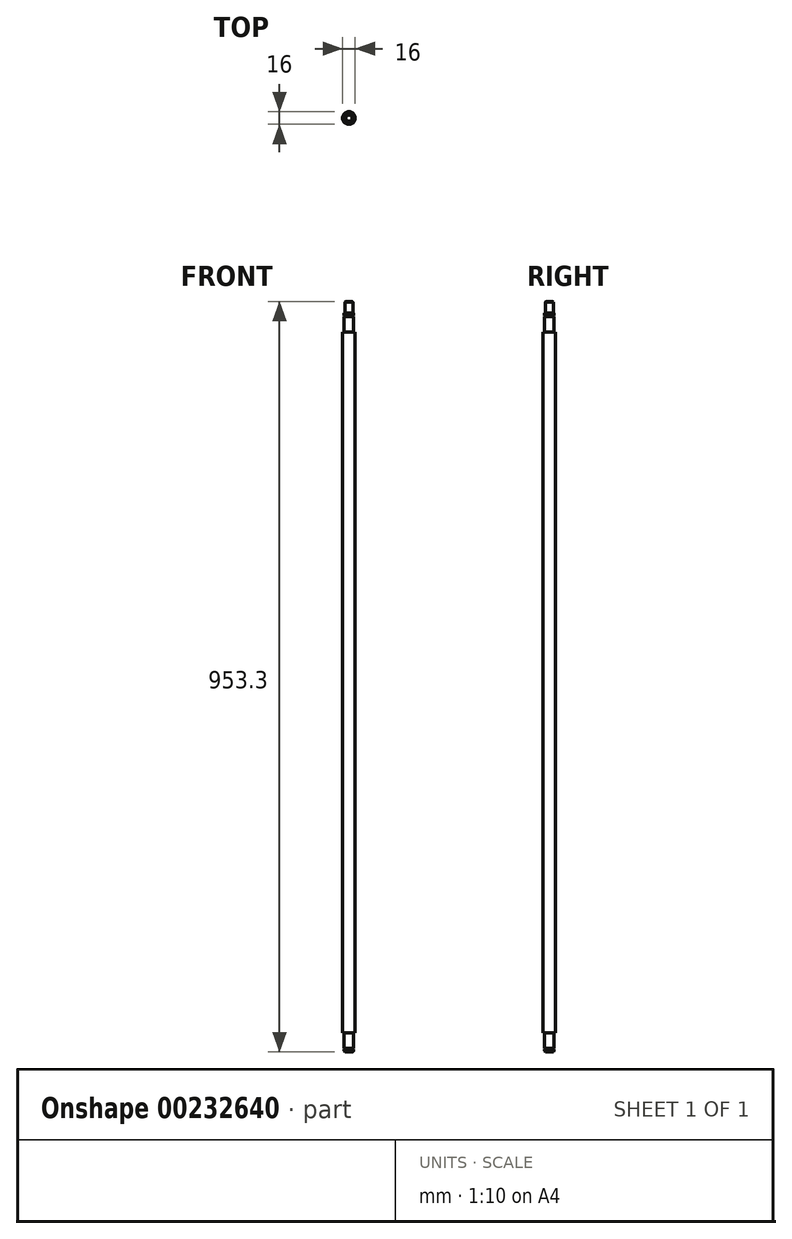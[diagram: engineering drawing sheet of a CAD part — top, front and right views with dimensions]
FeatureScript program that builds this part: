
annotation { "Feature Type Name" : "Feature", "Feature Type Description" : "" }
export const myFeature = defineFeature(function(context is Context, id is Id, definition is map)
    precondition{}
    {
        {
            var Q0;
            Q0=qCreatedBy(makeId("Top.planeOp"),FACE);
            var sketch = newSketch(context, id + "F0", { "sketchPlane" : qUnion([Q0])});
            skCircle(sketch, "E0", {"center": v(0, 0) * mm, "radius": 6 * mm});
            skSolve(sketch);
        }
        {
            var Q0;
            Q0=makeQuery(id+"F0.imprint","IMPRINT",FACE,{"disambiguationData":[TD([[makeQuery(id+"F0.imprint","IMPRINT",EDGE,{"derivedFrom":sQuery(id+"F0.wireOp",EDGE,"E0")}),1.0]])]});
            extrude(context, id + "F1", {"entities" : qUnion([Q0]), "depth" : 3 * mm});
        }
        {
            var Q0;
            Q0=makeQuery(id+"F1.opExtrude","CAP_FACE",FACE,{"disambiguationData":[OSD([sQuery(id+"F0.wireOp",EDGE,"E0")])],"isStart":false});
            var sketch = newSketch(context, id + "F2", { "sketchPlane" : qUnion([Q0])});
            skCircle(sketch, "E1", {"center": v(0, 0) * mm, "radius": 4.8 * mm});
            skSolve(sketch);
        }
        {
            var Q0;
            Q0=makeQuery(id+"F2.imprint","IMPRINT",FACE,{"disambiguationData":[TD([[makeQuery(id+"F2.imprint","IMPRINT",EDGE,{"derivedFrom":sQuery(id+"F2.wireOp",EDGE,"E1")}),1.0]])]});
            extrude(context, id + "F3", {"entities" : qUnion([Q0]), "operationType" : NewBodyOperationType.ADD, "depth" : 1.15 * mm});
        }
        {
            var Q0;
            Q0=makeQuery(id+"F3.opExtrude","CAP_FACE",FACE,{"disambiguationData":[OSD([sQuery(id+"F2.wireOp",EDGE,"E1")])],"isStart":false});
            var sketch = newSketch(context, id + "F4", { "sketchPlane" : qUnion([Q0])});
            skCircle(sketch, "E2", {"center": v(0, 0) * mm, "radius": 6 * mm});
            skSolve(sketch);
        }
        {
            var Q0;
            Q0=makeQuery(id+"F4.imprint","IMPRINT",FACE,{"disambiguationData":[TD([[makeQuery(id+"F4.imprint","IMPRINT",EDGE,{"derivedFrom":sQuery(id+"F4.wireOp",EDGE,"E2")}),1.0]])]});
            var Q1;
            Q1=makeQuery(id+"F4.imprint","IMPRINT",FACE,{"disambiguationData":[TD([[makeQuery(id+"F4.imprint","IMPRINT",EDGE,{"derivedFrom":makeQuery(id+"F3.opExtrude","CAP_EDGE",EDGE,{"disambiguationData":[OSD([sQuery(id+"F2.wireOp",EDGE,"E1")])],"isStart":false})}),1.0]])]});
            extrude(context, id + "F5", {"entities" : qUnion([Q0, Q1]), "operationType" : NewBodyOperationType.ADD, "depth" : 20 * mm});
        }
        {
            var Q0;
            Q0=makeQuery(id+"F5.opExtrude","CAP_FACE",FACE,{"disambiguationData":[OSD([sQuery(id+"F4.wireOp",EDGE,"E2")])],"isStart":false});
            var sketch = newSketch(context, id + "F6", { "sketchPlane" : qUnion([Q0])});
            skCircle(sketch, "E3", {"center": v(0, 0) * mm, "radius": 8 * mm});
            skSolve(sketch);
        }
        {
            var Q0;
            Q0=makeQuery(id+"F6.imprint","IMPRINT",FACE,{"disambiguationData":[TD([[makeQuery(id+"F6.imprint","IMPRINT",EDGE,{"derivedFrom":sQuery(id+"F6.wireOp",EDGE,"E3")}),1.0]])]});
            var Q1;
            Q1=makeQuery(id+"F6.imprint","IMPRINT",FACE,{"disambiguationData":[TD([[makeQuery(id+"F6.imprint","IMPRINT",EDGE,{"derivedFrom":makeQuery(id+"F5.opExtrude","CAP_EDGE",EDGE,{"disambiguationData":[OSD([sQuery(id+"F4.wireOp",EDGE,"E2")])],"isStart":false})}),1.0]])]});
            extrude(context, id + "F7", {"entities" : qUnion([Q0, Q1]), "operationType" : NewBodyOperationType.ADD, "depth" : 890 * mm});
        }
        {
            var Q0;
            Q0=makeQuery(id+"F7.opExtrude","CAP_FACE",FACE,{"disambiguationData":[OSD([sQuery(id+"F6.wireOp",EDGE,"E3")])],"isStart":false});
            var sketch = newSketch(context, id + "F8", { "sketchPlane" : qUnion([Q0])});
            skCircle(sketch, "E4", {"center": v(0, 0) * mm, "radius": 6 * mm});
            skSolve(sketch);
        }
        {
            var Q0;
            Q0=makeQuery(id+"F8.imprint","IMPRINT",FACE,{"disambiguationData":[TD([[makeQuery(id+"F8.imprint","IMPRINT",EDGE,{"derivedFrom":sQuery(id+"F8.wireOp",EDGE,"E4")}),1.0]])]});
            extrude(context, id + "F9", {"entities" : qUnion([Q0]), "operationType" : NewBodyOperationType.ADD, "depth" : 20 * mm});
        }
        {
            var Q0;
            Q0=makeQuery(id+"F9.opExtrude","CAP_FACE",FACE,{"disambiguationData":[OSD([sQuery(id+"F8.wireOp",EDGE,"E4")])],"isStart":false});
            var sketch = newSketch(context, id + "F10", { "sketchPlane" : qUnion([Q0])});
            skCircle(sketch, "E5", {"center": v(0, 0) * mm, "radius": 4.8 * mm});
            skSolve(sketch);
        }
        {
            var Q0;
            Q0=makeQuery(id+"F10.imprint","IMPRINT",FACE,{"disambiguationData":[TD([[makeQuery(id+"F10.imprint","IMPRINT",EDGE,{"derivedFrom":sQuery(id+"F10.wireOp",EDGE,"E5")}),1.0]])]});
            extrude(context, id + "F11", {"entities" : qUnion([Q0]), "operationType" : NewBodyOperationType.ADD, "depth" : 1.15 * mm});
        }
        {
            var Q0;
            Q0=makeQuery(id+"F11.opExtrude","CAP_FACE",FACE,{"disambiguationData":[OSD([sQuery(id+"F10.wireOp",EDGE,"E5")])],"isStart":false});
            var sketch = newSketch(context, id + "F12", { "sketchPlane" : qUnion([Q0])});
            skCircle(sketch, "E6", {"center": v(0, 0) * mm, "radius": 6 * mm});
            skSolve(sketch);
        }
        {
            var Q0;
            Q0=makeQuery(id+"F12.imprint","IMPRINT",FACE,{"disambiguationData":[TD([[makeQuery(id+"F12.imprint","IMPRINT",EDGE,{"derivedFrom":makeQuery(id+"F11.opExtrude","CAP_EDGE",EDGE,{"disambiguationData":[OSD([sQuery(id+"F10.wireOp",EDGE,"E5")])],"isStart":false})}),1.0]])]});
            var Q1;
            Q1=makeQuery(id+"F12.imprint","IMPRINT",FACE,{"disambiguationData":[TD([[makeQuery(id+"F12.imprint","IMPRINT",EDGE,{"derivedFrom":sQuery(id+"F12.wireOp",EDGE,"E6")}),1.0]])]});
            extrude(context, id + "F13", {"entities" : qUnion([Q0, Q1]), "operationType" : NewBodyOperationType.ADD, "depth" : 3 * mm});
        }
        {
            var Q0;
            Q0=makeQuery(id+"F13.opExtrude","CAP_FACE",FACE,{"disambiguationData":[OSD([sQuery(id+"F12.wireOp",EDGE,"E6")])],"isStart":false});
            var sketch = newSketch(context, id + "F14", { "sketchPlane" : qUnion([Q0])});
            skCircle(sketch, "E7", {"center": v(0, 0) * mm, "radius": 5 * mm});
            skSolve(sketch);
        }
        {
            var Q0;
            Q0=makeQuery(id+"F14.imprint","IMPRINT",FACE,{"disambiguationData":[TD([[makeQuery(id+"F14.imprint","IMPRINT",EDGE,{"derivedFrom":sQuery(id+"F14.wireOp",EDGE,"E7")}),1.0]])]});
            extrude(context, id + "F15", {"entities" : qUnion([Q0]), "operationType" : NewBodyOperationType.ADD, "depth" : 15 * mm});
        }
        {
            var Q0;
            Q0=makeQuery(id+"F15.opExtrude","CAP_EDGE",EDGE,{"disambiguationData":[OSD([sQuery(id+"F14.wireOp",EDGE,"E7")])],"isStart":false});
            var Q1;
            Q1=makeQuery(id+"F1.opExtrude","CAP_EDGE",EDGE,{"disambiguationData":[OSD([sQuery(id+"F0.wireOp",EDGE,"E0")])],"isStart":true});
            chamfer(context, id + "F16", {"entities" : qUnion([Q0, Q1]), "width" : 1 * mm, "tangentPropagation" : true});
        }
    });
